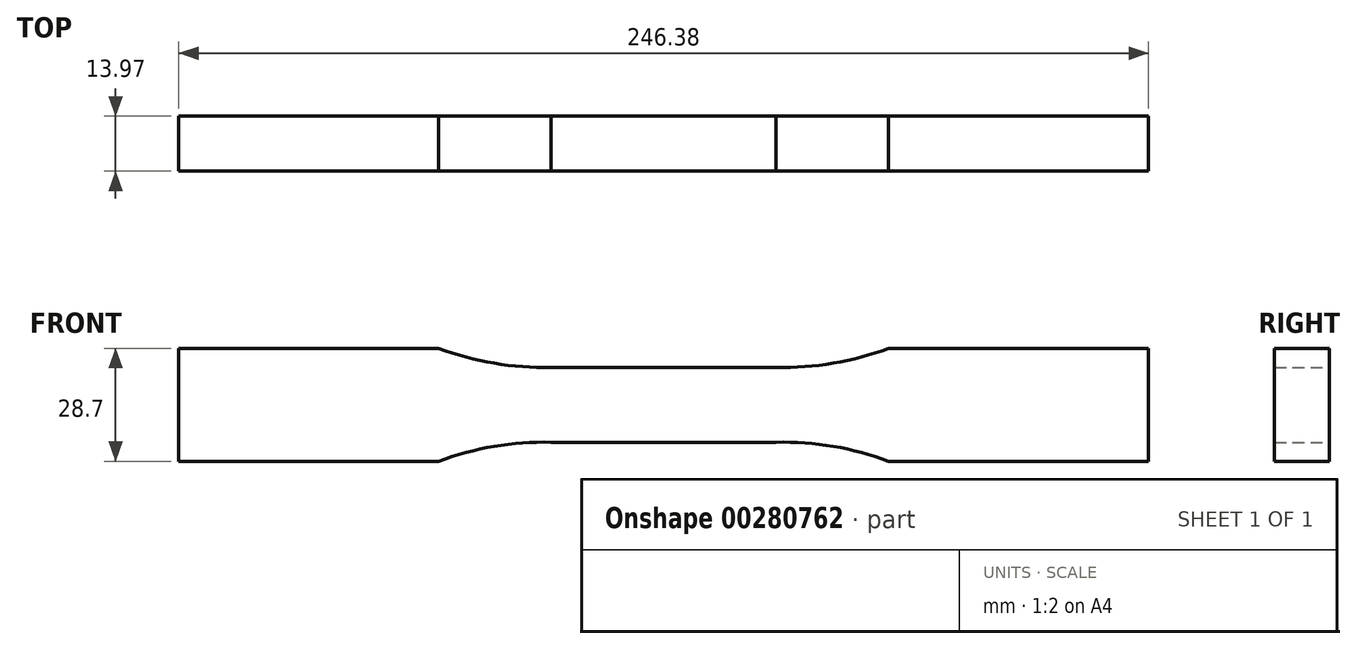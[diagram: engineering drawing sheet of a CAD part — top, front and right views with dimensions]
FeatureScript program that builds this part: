
annotation { "Feature Type Name" : "Feature", "Feature Type Description" : "" }
export const myFeature = defineFeature(function(context is Context, id is Id, definition is map)
    precondition{}
    {
        {
            var Q0;
            Q0=qCreatedBy(makeId("Front.planeOp"),FACE);
            var sketch = newSketch(context, id + "F0", { "sketchPlane" : qUnion([Q0])});
            skLineSegment(sketch, "E0", {"start": v(0, 9.53) * mm, "end": v(28.58, 9.53) * mm});
            skLineSegment(sketch, "E1", {"start": v(57.15, 14.35) * mm, "end": v(123.2, 14.35) * mm});
            skLineSegment(sketch, "E2.MirrorCS", {"start": v(0, -9.53) * mm, "end": v(28.58, -9.53) * mm});
            skLineSegment(sketch, "E3.MirrorCS", {"start": v(57.15, -14.35) * mm, "end": v(123.2, -14.35) * mm});
            skLineSegment(sketch, "E4.MirrorCS", {"start": v(-57.15, -14.35) * mm, "end": v(-123.2, -14.35) * mm});
            skLineSegment(sketch, "E5.MirrorCS", {"start": v(-57.15, 14.35) * mm, "end": v(-123.2, 14.35) * mm});
            skLineSegment(sketch, "E6.MirrorCS", {"start": v(0, -9.52) * mm, "end": v(-28.58, -9.52) * mm});
            skLineSegment(sketch, "E7.MirrorCS", {"start": v(0, 9.53) * mm, "end": v(-28.58, 9.53) * mm});
            skLineSegment(sketch, "E8", {"start": v(-123.2, 14.35) * mm, "end": v(-123.2, -14.35) * mm});
            skLineSegment(sketch, "E9", {"start": v(123.2, 14.35) * mm, "end": v(123.2, -14.35) * mm});
            skArc(sketch, "E10", {"start": v(-57.15, 14.35) * mm, "mid": v(-43.1, 10.57) * mm, "end": v(-28.57, 9.52) * mm});
            skArc(sketch, "E11", {"start": v(-28.57, -9.52) * mm, "mid": v(-43.1, -10.57) * mm, "end": v(-57.15, -14.35) * mm});
            skArc(sketch, "E12", {"start": v(28.58, 9.52) * mm, "mid": v(43.1, 10.57) * mm, "end": v(57.15, 14.35) * mm});
            skArc(sketch, "E13", {"start": v(57.15, -14.35) * mm, "mid": v(43.1, -10.57) * mm, "end": v(28.57, -9.53) * mm});
            skSolve(sketch);
        }
        {
            var Q0;
            Q0 = qSketchRegion(id + "F0", true);
            extrude(context, id + "F1", {"entities" : qUnion([Q0]), "depth" : 13.97 * mm});
        }
    });
